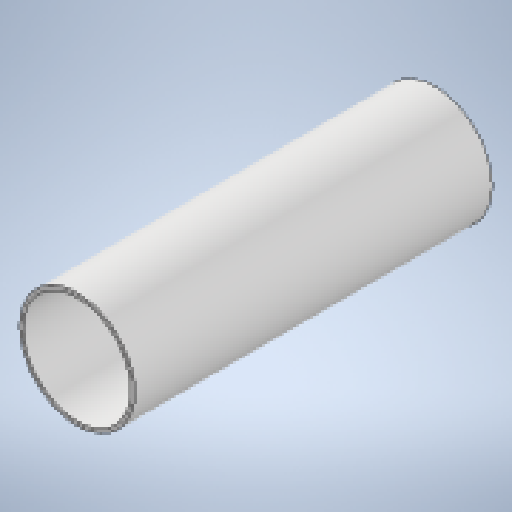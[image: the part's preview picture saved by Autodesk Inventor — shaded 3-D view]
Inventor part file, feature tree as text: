
AUTODESK INVENTOR PART (.ipt)
format: ipt  version: 2025.1 (Build 291241020, 241B)  size: 143,872 bytes
history: native  units: mm
features: extrude x1, sketch x1
ambient origin geometry x8: Origin, YZ Plane, XZ Plane, XY Plane, X Axis, Y Axis, Z Axis, Center Point
bodies: Solid1 (feature_tree)
feature tree (2):
  extrude  "Extrusion1"  Depth=280.0mm
  sketch  "Sketch1"  dims[d0=90.0mm d1=3.0mm d2=280.0mm d3=0.0mm]
